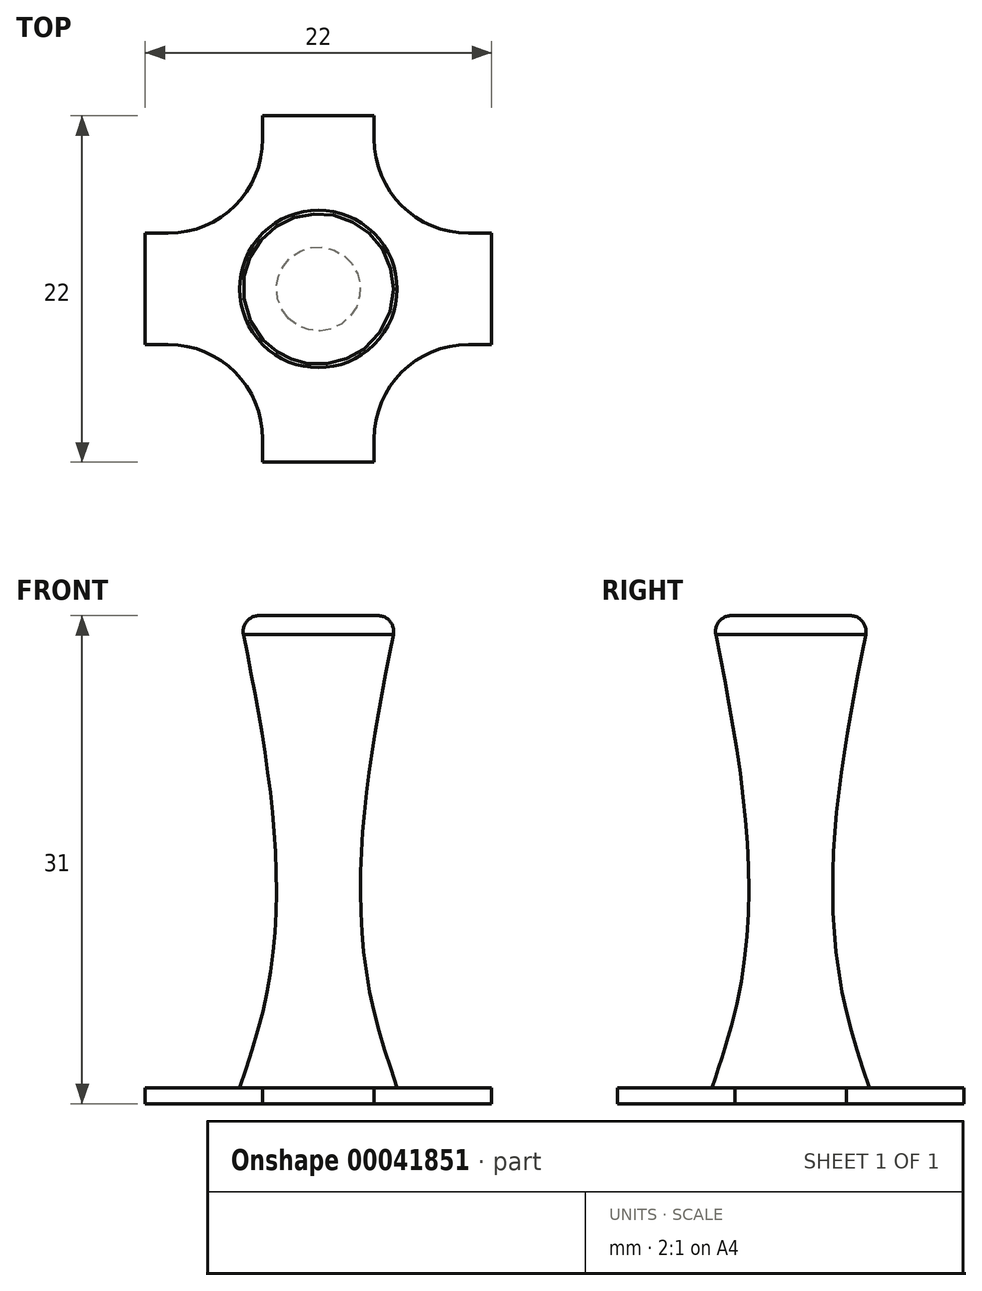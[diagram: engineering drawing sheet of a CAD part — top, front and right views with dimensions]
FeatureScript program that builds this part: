
annotation { "Feature Type Name" : "Feature", "Feature Type Description" : "" }
export const myFeature = defineFeature(function(context is Context, id is Id, definition is map)
    precondition{}
    {
        {
            var Q0;
            Q0=qCreatedBy(makeId("Top.planeOp"),FACE);
            var sketch = newSketch(context, id + "F0", { "sketchPlane" : qUnion([Q0])});
            skCircle(sketch, "E0", {"center": v(0, 0) * mm, "radius": 5 * mm});
            skSolve(sketch);
        }
        {
            var Q0;
            Q0=qCreatedBy(makeId("Top.planeOp"),FACE);
            cPlane(context, id + "F1", {"entities" : qUnion([Q0]), "cplaneType" : CPlaneType.OFFSET, "offset" : 5 * mm, "width" : 150 * mm, "height" : 150 * mm});
        }
        {
            var Q0;
            Q0=qCreatedBy(id+"F1.planeOp",FACE);
            var sketch = newSketch(context, id + "F2", { "sketchPlane" : qUnion([Q0])});
            skCircle(sketch, "E1", {"center": v(0, 0) * mm, "radius": 3.5 * mm});
            skSolve(sketch);
        }
        {
            var Q0;
            Q0=qCreatedBy(id+"F1.planeOp",FACE);
            cPlane(context, id + "F3", {"entities" : qUnion([Q0]), "cplaneType" : CPlaneType.OFFSET, "offset" : 10 * mm, "width" : 150 * mm, "height" : 150 * mm});
        }
        {
            var Q0;
            Q0=qCreatedBy(id+"F3.planeOp",FACE);
            cPlane(context, id + "F4", {"entities" : qUnion([Q0]), "cplaneType" : CPlaneType.OFFSET, "offset" : 10 * mm, "width" : 150 * mm, "height" : 150 * mm});
        }
        {
            var Q0;
            Q0=qCreatedBy(id+"F4.planeOp",FACE);
            cPlane(context, id + "F5", {"entities" : qUnion([Q0]), "cplaneType" : CPlaneType.OFFSET, "offset" : 5 * mm, "width" : 150 * mm, "height" : 150 * mm});
        }
        {
            var Q0;
            Q0=qCreatedBy(id+"F5.planeOp",FACE);
            var sketch = newSketch(context, id + "F6", { "sketchPlane" : qUnion([Q0])});
            skCircle(sketch, "E2", {"center": v(0, 0) * mm, "radius": 5 * mm});
            skSolve(sketch);
        }
        {
            var Q0;
            Q0=makeQuery(id+"F0.imprint","IMPRINT",FACE,{"disambiguationData":[TD([[makeQuery(id+"F0.imprint","IMPRINT",EDGE,{"derivedFrom":sQuery(id+"F0.wireOp",EDGE,"E0")}),1.0]])]});
            var Q1;
            Q1=makeQuery(id+"F2.imprint","IMPRINT",FACE,{"disambiguationData":[TD([[makeQuery(id+"F2.imprint","IMPRINT",EDGE,{"derivedFrom":sQuery(id+"F2.wireOp",EDGE,"E1")}),1.0]])]});
            var Q2;
            Q2=makeQuery(id+"F6.imprint","IMPRINT",FACE,{"disambiguationData":[TD([[makeQuery(id+"F6.imprint","IMPRINT",EDGE,{"derivedFrom":sQuery(id+"F6.wireOp",EDGE,"E2")}),1.0]])]});
            loft(context, id + "F7", {"sheetProfilesArray" : [{ "sheetProfileEntities" : qUnion([Q0]) }, { "sheetProfileEntities" : qUnion([Q1]) }, { "sheetProfileEntities" : qUnion([Q2]) }]});
        }
        {
            var Q0;
            Q0=makeQuery(id+"F7.opLoft","MID_CAP_EDGE",EDGE,{"disambiguationData":[OSD([sQuery(id+"F0.wireOp",EDGE,"E0"),sQuery(id+"F6.wireOp",EDGE,"E2")])],"capPos":2.0});
            fillet(context, id + "F8", {"entities" : qUnion([Q0]), "radius" : 1 * mm, "tangentPropagation" : true, "allowEdgeOverflow" : false});
        }
        {
            var Q0;
            Q0=qCreatedBy(makeId("Top.planeOp"),FACE);
            var sketch = newSketch(context, id + "F9", { "sketchPlane" : qUnion([Q0])});
            skCircle(sketch, "E3", {"center": v(0, 0) * mm, "radius": 5 * mm});
            skPoint(sketch, "E4", {"position": v(0, 5) * mm});
            skPoint(sketch, "E5", {"position": v(-5, 0) * mm});
            skLineSegment(sketch, "E6", {"start": v(0, 0) * mm, "end": v(-3.54, 3.54) * mm});
            skPoint(sketch, "E7", {"position": v(-3.54, 3.54) * mm});
            skLineSegment(sketch, "E8", {"start": v(-3.54, 3.54) * mm, "end": v(-3.54, 11) * mm});
            skLineSegment(sketch, "E9", {"start": v(-3.54, 11) * mm, "end": v(0, 11) * mm});
            skLineSegment(sketch, "E10", {"start": v(0, 11) * mm, "end": v(0, 5) * mm});
            skLineSegment(sketch, "E11", {"start": v(-3.54, 3.54) * mm, "end": v(-11, 3.54) * mm});
            skLineSegment(sketch, "E12", {"start": v(-11, 3.54) * mm, "end": v(-11, 0) * mm});
            skLineSegment(sketch, "E13", {"start": v(-11, 0) * mm, "end": v(-5, 0) * mm});
            skLineSegment(sketch, "E14.MirrorCS", {"start": v(3.54, 11) * mm, "end": v(0, 11) * mm});
            skLineSegment(sketch, "E15.MirrorCS", {"start": v(3.54, 3.54) * mm, "end": v(3.54, 11) * mm});
            skLineSegment(sketch, "E16.MirrorCS", {"start": v(3.54, 3.54) * mm, "end": v(11, 3.54) * mm});
            skLineSegment(sketch, "E17.MirrorCS", {"start": v(11, 0) * mm, "end": v(5, 0) * mm});
            skLineSegment(sketch, "E18.MirrorCS", {"start": v(11, 3.54) * mm, "end": v(11, 0) * mm});
            skLineSegment(sketch, "E19.MirrorCS", {"start": v(11, -3.54) * mm, "end": v(11, 0) * mm});
            skLineSegment(sketch, "E20.MirrorCS", {"start": v(3.54, -3.54) * mm, "end": v(11, -3.54) * mm});
            skLineSegment(sketch, "E21.MirrorCS", {"start": v(3.54, -3.54) * mm, "end": v(3.54, -11) * mm});
            skLineSegment(sketch, "E22.MirrorCS", {"start": v(3.54, -11) * mm, "end": v(0, -11) * mm});
            skLineSegment(sketch, "E23.MirrorCS", {"start": v(-3.54, -11) * mm, "end": v(0, -11) * mm});
            skLineSegment(sketch, "E24.MirrorCS", {"start": v(-3.54, -3.54) * mm, "end": v(-3.54, -11) * mm});
            skLineSegment(sketch, "E25.MirrorCS", {"start": v(-3.54, -3.54) * mm, "end": v(-11, -3.54) * mm});
            skLineSegment(sketch, "E26.MirrorCS", {"start": v(-11, -3.54) * mm, "end": v(-11, 0) * mm});
            skSolve(sketch);
        }
        {
            var Q0;
            Q0 = qSketchRegion(id + "F9", true);
            extrude(context, id + "F10", {"entities" : qUnion([Q0]), "operationType" : NewBodyOperationType.ADD, "oppositeDirection" : true, "depth" : 1 * mm});
        }
        {
            var Q0;
            Q0=makeQuery(id+"F10.opExtrude","SWEPT_EDGE",EDGE,{"disambiguationData":[OSD([sQuery(id+"F9.wireOp",EDGE,"E3"),sQuery(id+"F9.wireOp",EDGE,"E24.MirrorCS"),sQuery(id+"F9.wireOp",EDGE,"E25.MirrorCS")])]});
            var Q1;
            Q1=makeQuery(id+"F10.opExtrude","SWEPT_EDGE",EDGE,{"disambiguationData":[OSD([sQuery(id+"F9.wireOp",EDGE,"E3"),sQuery(id+"F9.wireOp",EDGE,"E20.MirrorCS"),sQuery(id+"F9.wireOp",EDGE,"E21.MirrorCS")])]});
            var Q2;
            Q2=makeQuery(id+"F10.opExtrude","SWEPT_EDGE",EDGE,{"disambiguationData":[OSD([sQuery(id+"F9.wireOp",EDGE,"E3"),sQuery(id+"F9.wireOp",EDGE,"E15.MirrorCS"),sQuery(id+"F9.wireOp",EDGE,"E16.MirrorCS")])]});
            var Q3;
            Q3=makeQuery(id+"F10.opExtrude","SWEPT_EDGE",EDGE,{"disambiguationData":[OSD([sQuery(id+"F9.wireOp",EDGE,"E3"),sQuery(id+"F9.wireOp",EDGE,"E8"),sQuery(id+"F9.wireOp",EDGE,"E11")])]});
            fillet(context, id + "F11", {"entities" : qUnion([Q0, Q1, Q2, Q3]), "radius" : 6 * mm, "tangentPropagation" : true, "allowEdgeOverflow" : false});
        }
    });
